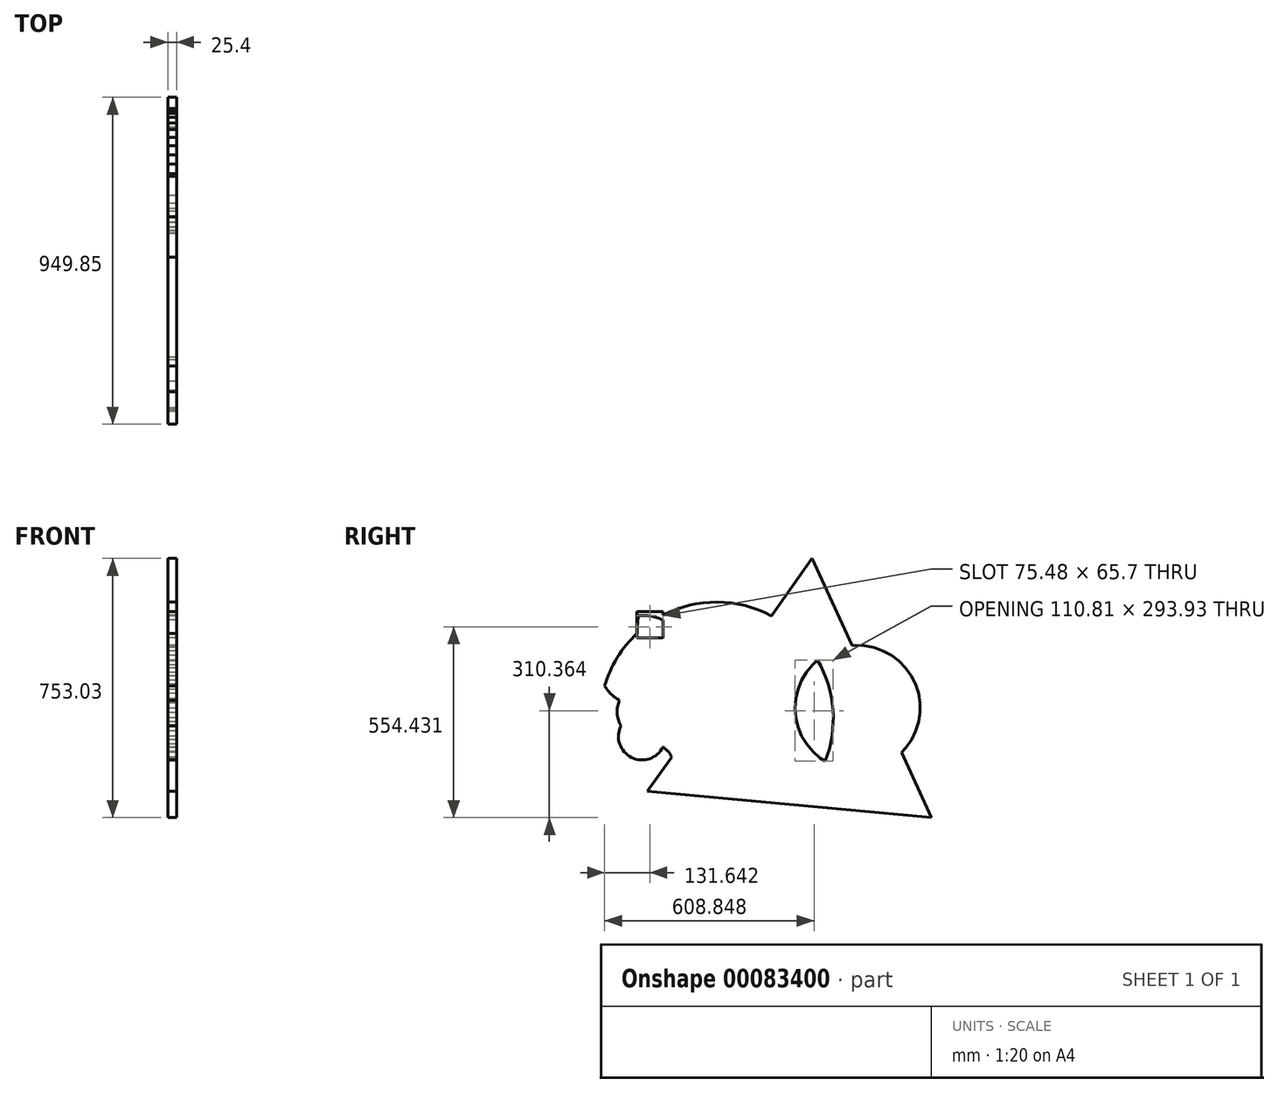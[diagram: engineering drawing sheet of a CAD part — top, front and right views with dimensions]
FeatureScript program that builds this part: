
annotation { "Feature Type Name" : "Feature", "Feature Type Description" : "" }
export const myFeature = defineFeature(function(context is Context, id is Id, definition is map)
    precondition{}
    {
        {
            var Q0;
            Q0=qCreatedBy(makeId("Right.planeOp"),FACE);
            var sketch = newSketch(context, id + "F0", { "sketchPlane" : qUnion([Q0])});
            skLineSegment(sketch, "E0", {"start": v(0, 76.76) * mm, "end": v(75.48, 76.76) * mm});
            skLineSegment(sketch, "E1", {"start": v(75.48, 76.76) * mm, "end": v(75.48, 0) * mm});
            skLineSegment(sketch, "E2", {"start": v(75.48, 0) * mm, "end": v(0, 0) * mm});
            skLineSegment(sketch, "E3", {"start": v(0, 0) * mm, "end": v(0, 76.76) * mm});
            skLineSegment(sketch, "E4", {"start": v(0, 0) * mm, "end": v(-23.1, -40.66) * mm});
            skArc(sketch, "E5", {"start": v(86.7, 296.27) * mm, "mid": v(22.12, 154.35) * mm, "end": v(0, 0) * mm});
            skArc(sketch, "E6", {"start": v(-75.58, 27.73) * mm, "mid": v(96.47, -174.02) * mm, "end": v(-45.81, 49.73) * mm});
            skArc(sketch, "E7", {"start": v(0, -134.44) * mm, "mid": v(-57.38, -218.04) * mm, "end": v(7.77, -295.73) * mm});
            skArc(sketch, "E8", {"start": v(58, -232.62) * mm, "mid": v(-35.27, -332.56) * mm, "end": v(70.65, -246.14) * mm});
            skArc(sketch, "E9", {"start": v(76, -316.48) * mm, "mid": v(157.47, -355) * mm, "end": v(245.05, -333.79) * mm});
            skArc(sketch, "E10", {"start": v(171.25, -220.42) * mm, "mid": v(101.43, -346.58) * mm, "end": v(245.05, -333.79) * mm});
            skArc(sketch, "E11", {"start": v(45.45, -517.9) * mm, "mid": v(481.34, -5.32) * mm, "end": v(-66.73, -395.65) * mm});
            skCircle(sketch, "E12.cCircle", {"center": v(465.03, -245.26) * mm, "radius": 239.36 * mm, "construction": true});
            skLineSegment(sketch, "E12.0", {"start": v(30.27, -445.65) * mm, "end": v(508.87, 231.45) * mm});
            skLineSegment(sketch, "E12.1", {"start": v(508.87, 231.45) * mm, "end": v(855.95, -521.58) * mm});
            skLineSegment(sketch, "E12.2", {"start": v(855.95, -521.58) * mm, "end": v(30.27, -445.65) * mm});
            skPoint(sketch, "E12.0.midPoint", {"position": v(269.57, -107.1) * mm});
            skCircle(sketch, "E13.cCircle", {"center": v(641.4, -203.17) * mm, "radius": 181.33 * mm, "construction": true});
            skLineSegment(sketch, "E13.0", {"start": v(468.26, -258.8) * mm, "end": v(461.8, -231.72) * mm});
            skLineSegment(sketch, "E13.1", {"start": v(461.8, -231.72) * mm, "end": v(459.54, -203.97) * mm});
            skLineSegment(sketch, "E13.2", {"start": v(459.54, -203.97) * mm, "end": v(461.55, -176.2) * mm});
            skLineSegment(sketch, "E13.3", {"start": v(461.55, -176.2) * mm, "end": v(467.78, -149.06) * mm});
            skLineSegment(sketch, "E13.4", {"start": v(467.78, -149.06) * mm, "end": v(478.07, -123.2) * mm});
            skLineSegment(sketch, "E13.5", {"start": v(478.07, -123.2) * mm, "end": v(492.2, -99.2) * mm});
            skLineSegment(sketch, "E13.6", {"start": v(492.2, -99.2) * mm, "end": v(509.82, -77.64) * mm});
            skLineSegment(sketch, "E13.7", {"start": v(509.82, -77.64) * mm, "end": v(530.52, -59.02) * mm});
            skLineSegment(sketch, "E13.8", {"start": v(530.52, -59.02) * mm, "end": v(553.82, -43.79) * mm});
            skLineSegment(sketch, "E13.9", {"start": v(553.82, -43.79) * mm, "end": v(579.18, -32.29) * mm});
            skLineSegment(sketch, "E13.10", {"start": v(579.18, -32.29) * mm, "end": v(606, -24.8) * mm});
            skLineSegment(sketch, "E13.11", {"start": v(606, -24.8) * mm, "end": v(633.64, -21.48) * mm});
            skLineSegment(sketch, "E13.12", {"start": v(633.64, -21.48) * mm, "end": v(661.46, -22.42) * mm});
            skLineSegment(sketch, "E13.13", {"start": v(661.46, -22.42) * mm, "end": v(688.82, -27.6) * mm});
            skLineSegment(sketch, "E13.14", {"start": v(688.82, -27.6) * mm, "end": v(715.07, -36.9) * mm});
            skLineSegment(sketch, "E13.15", {"start": v(715.07, -36.9) * mm, "end": v(739.58, -50.1) * mm});
            skLineSegment(sketch, "E13.16", {"start": v(739.58, -50.1) * mm, "end": v(761.8, -66.87) * mm});
            skLineSegment(sketch, "E13.17", {"start": v(761.8, -66.87) * mm, "end": v(781.2, -86.85) * mm});
            skLineSegment(sketch, "E13.18", {"start": v(781.2, -86.85) * mm, "end": v(797.31, -109.55) * mm});
            skLineSegment(sketch, "E13.19", {"start": v(797.31, -109.55) * mm, "end": v(809.78, -134.45) * mm});
            skLineSegment(sketch, "E13.20", {"start": v(809.78, -134.45) * mm, "end": v(818.3, -160.95) * mm});
            skLineSegment(sketch, "E13.21", {"start": v(818.3, -160.95) * mm, "end": v(822.67, -188.45) * mm});
            skLineSegment(sketch, "E13.22", {"start": v(822.67, -188.45) * mm, "end": v(822.79, -216.3) * mm});
            skLineSegment(sketch, "E13.23", {"start": v(822.79, -216.3) * mm, "end": v(818.66, -243.83) * mm});
            skLineSegment(sketch, "E13.24", {"start": v(818.66, -243.83) * mm, "end": v(810.38, -270.41) * mm});
            skLineSegment(sketch, "E13.25", {"start": v(810.38, -270.41) * mm, "end": v(798.13, -295.42) * mm});
            skLineSegment(sketch, "E13.26", {"start": v(798.13, -295.42) * mm, "end": v(782.21, -318.26) * mm});
            skLineSegment(sketch, "E13.27", {"start": v(782.21, -318.26) * mm, "end": v(763, -338.4) * mm});
            skLineSegment(sketch, "E13.28", {"start": v(763, -338.4) * mm, "end": v(740.93, -355.38) * mm});
            skLineSegment(sketch, "E13.29", {"start": v(740.93, -355.38) * mm, "end": v(716.52, -368.79) * mm});
            skLineSegment(sketch, "E13.30", {"start": v(716.52, -368.79) * mm, "end": v(690.36, -378.32) * mm});
            skLineSegment(sketch, "E13.31", {"start": v(690.36, -378.32) * mm, "end": v(663.05, -383.74) * mm});
            skLineSegment(sketch, "E13.32", {"start": v(663.05, -383.74) * mm, "end": v(635.24, -384.93) * mm});
            skLineSegment(sketch, "E13.33", {"start": v(635.24, -384.93) * mm, "end": v(607.56, -381.85) * mm});
            skLineSegment(sketch, "E13.34", {"start": v(607.56, -381.85) * mm, "end": v(580.68, -374.6) * mm});
            skLineSegment(sketch, "E13.35", {"start": v(580.68, -374.6) * mm, "end": v(555.23, -363.32) * mm});
            skLineSegment(sketch, "E13.36", {"start": v(555.23, -363.32) * mm, "end": v(531.8, -348.29) * mm});
            skLineSegment(sketch, "E13.37", {"start": v(531.8, -348.29) * mm, "end": v(510.92, -329.85) * mm});
            skLineSegment(sketch, "E13.38", {"start": v(510.92, -329.85) * mm, "end": v(493.12, -308.45) * mm});
            skLineSegment(sketch, "E13.39", {"start": v(493.12, -308.45) * mm, "end": v(478.78, -284.58) * mm});
            skLineSegment(sketch, "E13.40", {"start": v(478.78, -284.58) * mm, "end": v(468.26, -258.8) * mm});
            skSolve(sketch);
        }
        {
            var Q0;
            Q0 = qSketchRegion(id + "F0", true);
            extrude(context, id + "F1", {"entities" : qUnion([Q0]), "depth" : 25.4 * mm});
        }
    });
